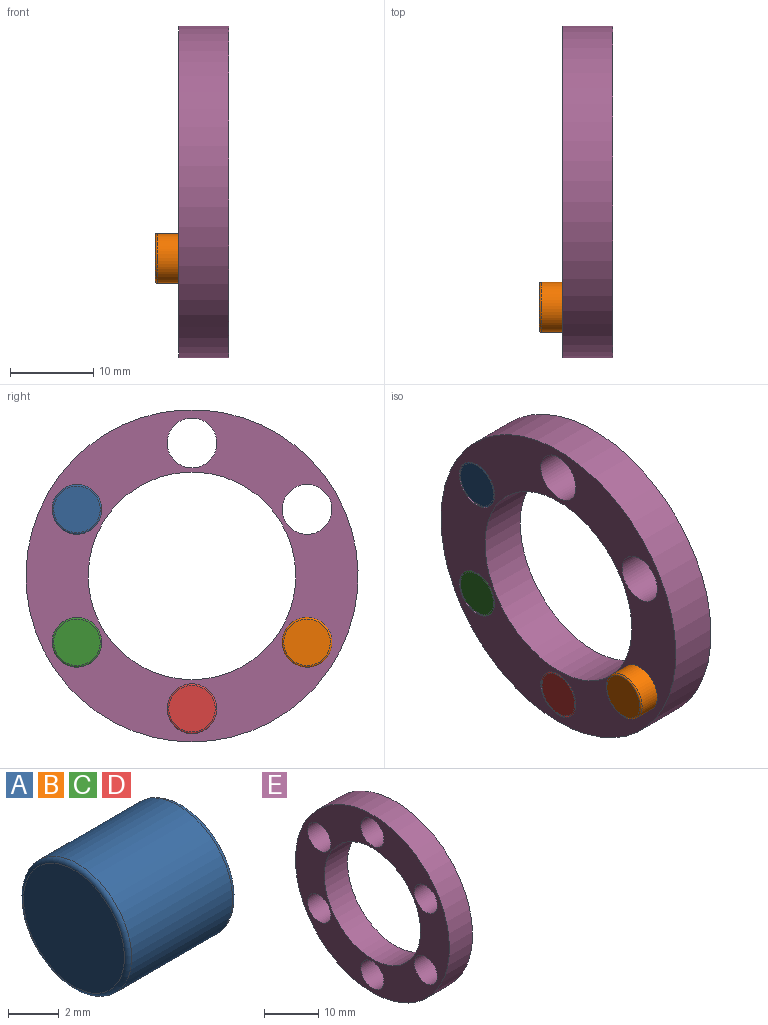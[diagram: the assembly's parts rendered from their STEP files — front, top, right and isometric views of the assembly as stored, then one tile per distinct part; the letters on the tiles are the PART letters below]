
ASSEMBLY  parts=5 mates=7
PART A: 5 faces, bbox 6x6.5x6.5 mm
  f0: cylinder r=3mm len=6mm, axis (-1,0,0), area 105.6mm2, adj f3,f4
  f1: plane 5.6x5.6mm, normal (1,0,0), area 24.6mm2, adj f4
  f2: plane 5.6x5.6mm, normal (-1,0,0), area 24.6mm2, adj f3
  f3: torus R=2.8mm, axis (1,0,0), area 5.8mm2, adj f0,f2
  f4: torus R=2.8mm, axis (1,0,0), area 5.8mm2, adj f0,f1
PART B: same geometry as A
PART C: same geometry as A
PART D: same geometry as A
PART E: 10 faces, bbox 6x40x40 mm
  f0: cylinder r=3mm len=6mm, axis (-1,0,0), area 113.1mm2, adj f8,f9
  f1: cylinder r=12.5mm len=25mm, axis (-1,0,0), area 471.2mm2, adj f8,f9
  f2: cylinder r=3mm len=6mm, axis (-1,0,0), area 113.1mm2, adj f8,f9
  f3: cylinder r=3mm len=6mm, axis (-1,0,0), area 113.1mm2, adj f8,f9
  f4: cylinder r=3mm len=6mm, axis (-1,0,0), area 113.1mm2, adj f8,f9
  f5: cylinder r=3mm len=6mm, axis (-1,0,0), area 113.1mm2, adj f8,f9
  f6: cylinder r=3mm len=6mm, axis (-1,0,0), area 113.1mm2, adj f8,f9
  f7: cylinder r=20mm len=40mm, axis (-1,0,0), area 754mm2, adj f8,f9
  f8: plane 40x40mm, normal (1,0,0), area 596.1mm2, adj f0,f1,f2,f3,f4,f5,f6,f7
  f9: plane 40x40mm, normal (-1,0,0), area 596.1mm2, adj f0,f1,f2,f3,f4,f5,f6,f7
PLACE A t=(0,13.86,8)mm
PLACE B t=(-2.8,-13.86,-8)mm
PLACE C t=(0,13.86,-8)mm
PLACE D t=(0,0,-16)mm
PLACE E at identity fixed
MATE cylindrical B.f0 <-> E.f4  axis (1,0,0) through (3,-13.86,-8)mm
MATE cylindrical D.f0 <-> E.f3  axis (-1,0,0) through (5.8,0,-16)mm
MATE cylindrical A.f0 <-> E.f0  axis (-1,0,0) through (3,13.86,8)mm
MATE cylindrical C.f0 <-> E.f2  axis (-1,0,0) through (5.8,13.86,-8)mm
MATE planar D.f0 <-> A.f0  axis (-1,0,0) through (0,0,-16)mm
MATE planar C.f0 <-> A.f0  axis (-1,0,0) through (0,13.86,-8)mm
MATE planar A.f0 <-> E.f7  axis (-1,0,0) through (0,13.86,8)mm
